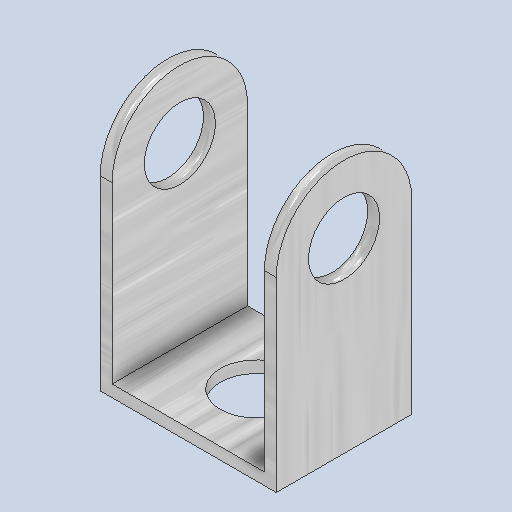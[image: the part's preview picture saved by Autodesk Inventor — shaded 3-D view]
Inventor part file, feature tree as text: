
AUTODESK INVENTOR PART (.ipt)
format: ipt  version: 2024 (Build 280153000, 153)  size: 311,296 bytes
history: native  units: mm
features: extrude x3, sketch x3, other x1
ambient origin geometry x8: Origin, YZ Plane, XZ Plane, XY Plane, X Axis, Y Axis, Z Axis, Center Point
bodies: Body1 (feature_tree)
feature tree (7):
  other  "솔리드1"
  extrude  "돌출1"  Depth=8.0mm
  extrude  "돌출2"  Depth=11.0mm
  extrude  "돌출3"  Depth=4.2mm
  sketch  "스케치1"
  sketch  "스케치2"
  sketch  "스케치3"
